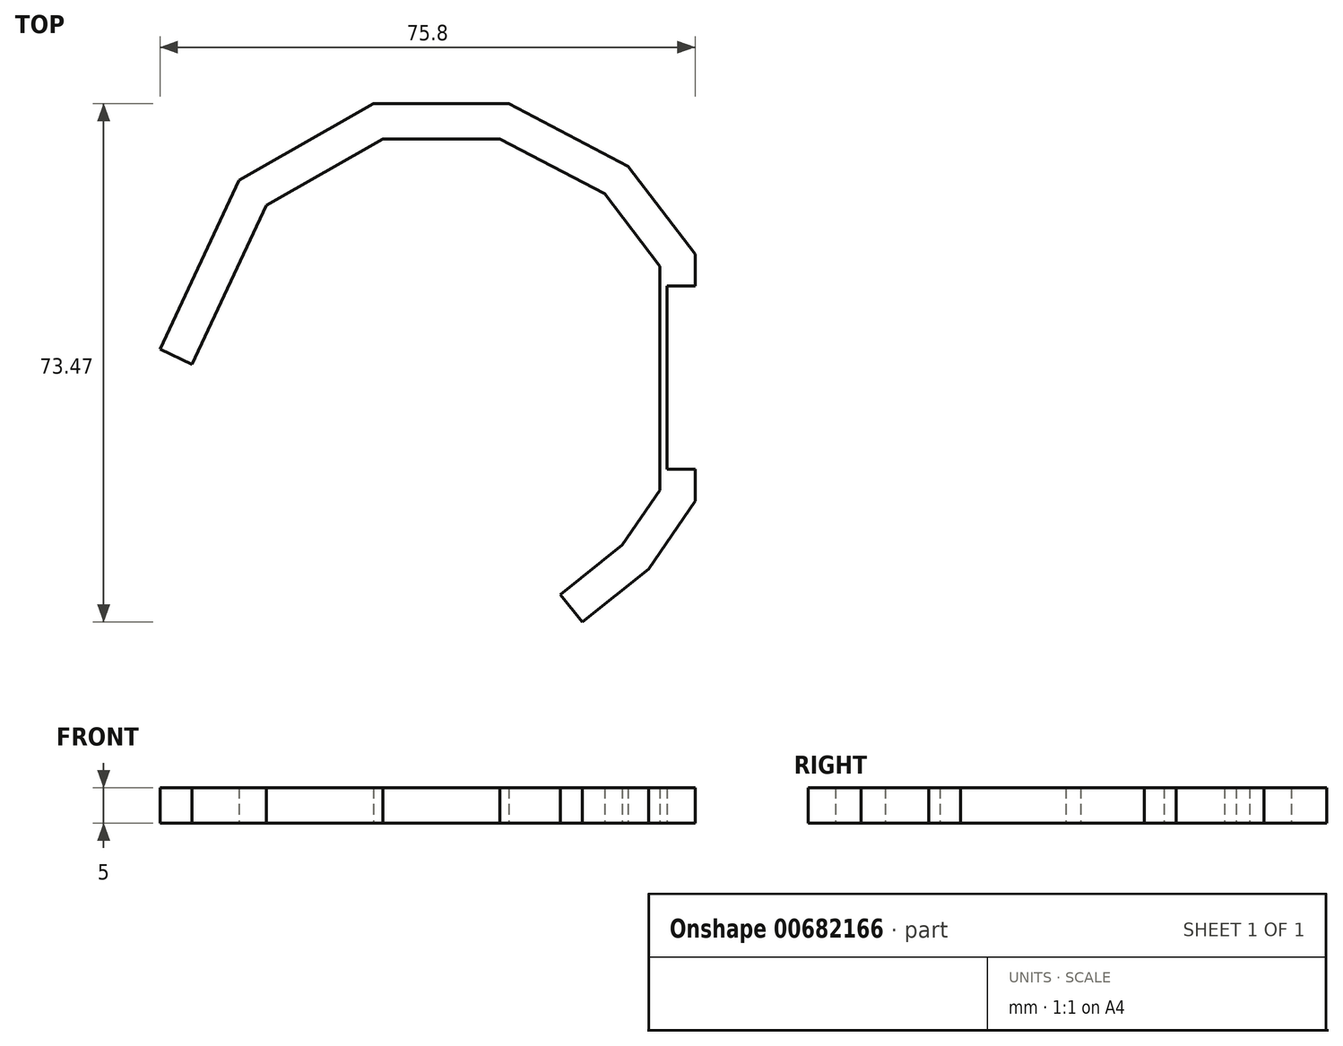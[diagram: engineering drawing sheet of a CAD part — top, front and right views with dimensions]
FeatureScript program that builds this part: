
annotation { "Feature Type Name" : "Feature", "Feature Type Description" : "" }
export const myFeature = defineFeature(function(context is Context, id is Id, definition is map)
    precondition{}
    {
        {
            var Q0;
            Q0=qCreatedBy(makeId("Top.planeOp"),FACE);
            var sketch = newSketch(context, id + "F0", { "sketchPlane" : qUnion([Q0])});
            skLineSegment(sketch, "E0", {"start": v(0, 0) * mm, "end": v(0, -35) * mm});
            skLineSegment(sketch, "E1", {"start": v(0, -35) * mm, "end": v(-6.6, -44.62) * mm});
            skLineSegment(sketch, "E2", {"start": v(-6.6, -44.62) * mm, "end": v(-15.99, -52.13) * mm});
            skLineSegment(sketch, "E3", {"start": v(0, 0) * mm, "end": v(-9.51, 12.47) * mm});
            skLineSegment(sketch, "E4", {"start": v(-9.51, 12.47) * mm, "end": v(-26.42, 21.34) * mm});
            skCircle(sketch, "E5", {"center": v(-36, -17.5) * mm, "radius": 40 * mm, "construction": true});
            skLineSegment(sketch, "E6", {"start": v(-26.42, 21.34) * mm, "end": v(-45.58, 21.34) * mm});
            skLineSegment(sketch, "E7", {"start": v(-45.58, 21.34) * mm, "end": v(-64.6, 10.47) * mm});
            skLineSegment(sketch, "E8", {"start": v(-64.6, 10.47) * mm, "end": v(-75.8, -13.47) * mm});
            skLineSegment(sketch, "E9.0", {"start": v(-60.74, 6.91) * mm, "end": v(-71.27, -15.59) * mm});
            skLineSegment(sketch, "E9.1", {"start": v(-44.25, 16.34) * mm, "end": v(-60.74, 6.91) * mm});
            skLineSegment(sketch, "E9.2", {"start": v(-27.65, 16.34) * mm, "end": v(-44.25, 16.34) * mm});
            skLineSegment(sketch, "E9.3", {"start": v(-12.81, 8.56) * mm, "end": v(-27.65, 16.34) * mm});
            skLineSegment(sketch, "E9.4", {"start": v(-10.3, -41.18) * mm, "end": v(-19.11, -48.23) * mm});
            skLineSegment(sketch, "E9.5", {"start": v(-5, -33.45) * mm, "end": v(-10.3, -41.18) * mm});
            skLineSegment(sketch, "E9.6", {"start": v(-5, -1.69) * mm, "end": v(-5, -33.45) * mm});
            skLineSegment(sketch, "E9.7", {"start": v(-5, -1.69) * mm, "end": v(-12.81, 8.56) * mm});
            skLineSegment(sketch, "E10", {"start": v(-75.8, -13.47) * mm, "end": v(-71.27, -15.59) * mm});
            skLineSegment(sketch, "E11", {"start": v(-19.11, -48.23) * mm, "end": v(-15.99, -52.13) * mm});
            skSolve(sketch);
        }
        {
            var Q0;
            Q0=makeQuery(id+"F0.imprint","IMPRINT",FACE,{"disambiguationData":[TD([[makeQuery(id+"F0.imprint","IMPRINT",EDGE,{"derivedFrom":sQuery(id+"F0.wireOp",EDGE,"E0")}),-1.0]])]});
            extrude(context, id + "F1", {"entities" : qUnion([Q0]), "depth" : 5 * mm, "offsetDistance" : 25 * mm});
        }
        {
            var Q0;
            Q0=makeQuery(id+"F1.opExtrude","SWEPT_FACE",FACE,{"disambiguationData":[OSD([sQuery(id+"F0.wireOp",EDGE,"E0")])]});
            var sketch = newSketch(context, id + "F2", { "sketchPlane" : qUnion([Q0])});
            skLineSegment(sketch, "E12", {"start": v(-4.5, 2.5) * mm, "end": v(-4.5, 5) * mm});
            skLineSegment(sketch, "E13", {"start": v(-4.5, 2.5) * mm, "end": v(-4.5, 0) * mm});
            skLineSegment(sketch, "E14", {"start": v(-30.5, 2.5) * mm, "end": v(-30.5, 0) * mm});
            skLineSegment(sketch, "E15", {"start": v(-30.5, 2.5) * mm, "end": v(-30.5, 5) * mm});
            skLineSegment(sketch, "E16", {"start": v(-30.5, 0) * mm, "end": v(-4.5, 0) * mm});
            skLineSegment(sketch, "E17", {"start": v(-30.5, 5) * mm, "end": v(-4.5, 5) * mm});
            skSolve(sketch);
        }
        {
            var Q0;
            Q0=makeQuery(id+"F2.imprint","IMPRINT",FACE,{"disambiguationData":[TD([[makeQuery(id+"F2.imprint","IMPRINT",EDGE,{"derivedFrom":sQuery(id+"F2.wireOp",EDGE,"E12")}),1.0]])]});
            extrude(context, id + "F3", {"entities" : qUnion([Q0]), "operationType" : NewBodyOperationType.REMOVE, "oppositeDirection" : true, "depth" : 4 * mm, "offsetDistance" : 25 * mm});
        }
        {
            var Q0;
            Q0=makeQuery(id+"F1.opExtrude","SWEPT_BODY",BODY,{"disambiguationData":[OSD([sQuery(id+"F0.wireOp",EDGE,"E0"),sQuery(id+"F0.wireOp",EDGE,"E1"),sQuery(id+"F0.wireOp",EDGE,"E2"),sQuery(id+"F0.wireOp",EDGE,"E3"),sQuery(id+"F0.wireOp",EDGE,"E4"),sQuery(id+"F0.wireOp",EDGE,"E6"),sQuery(id+"F0.wireOp",EDGE,"E7"),sQuery(id+"F0.wireOp",EDGE,"E8"),sQuery(id+"F0.wireOp",EDGE,"E9.0"),sQuery(id+"F0.wireOp",EDGE,"E9.1"),sQuery(id+"F0.wireOp",EDGE,"E9.2"),sQuery(id+"F0.wireOp",EDGE,"E9.3"),sQuery(id+"F0.wireOp",EDGE,"E9.4"),sQuery(id+"F0.wireOp",EDGE,"E9.5"),sQuery(id+"F0.wireOp",EDGE,"E9.6"),sQuery(id+"F0.wireOp",EDGE,"E9.7"),sQuery(id+"F0.wireOp",EDGE,"E10"),sQuery(id+"F0.wireOp",EDGE,"E11")])]});
            transform(context, id + "F4", {"entities" : qUnion([Q0]), "transformType" : TransformType.TRANSLATION_3D, "dx" : 0 * mm, "dy" : 0 * mm, "dz" : 0 * mm, "makeCopy" : true});
        }
        {
            var Q0;
            Q0=makeQuery(id+"F1.opExtrude","SWEPT_BODY",BODY,{"disambiguationData":[OSD([sQuery(id+"F0.wireOp",EDGE,"E0"),sQuery(id+"F0.wireOp",EDGE,"E1"),sQuery(id+"F0.wireOp",EDGE,"E2"),sQuery(id+"F0.wireOp",EDGE,"E3"),sQuery(id+"F0.wireOp",EDGE,"E4"),sQuery(id+"F0.wireOp",EDGE,"E6"),sQuery(id+"F0.wireOp",EDGE,"E7"),sQuery(id+"F0.wireOp",EDGE,"E8"),sQuery(id+"F0.wireOp",EDGE,"E9.0"),sQuery(id+"F0.wireOp",EDGE,"E9.1"),sQuery(id+"F0.wireOp",EDGE,"E9.2"),sQuery(id+"F0.wireOp",EDGE,"E9.3"),sQuery(id+"F0.wireOp",EDGE,"E9.4"),sQuery(id+"F0.wireOp",EDGE,"E9.5"),sQuery(id+"F0.wireOp",EDGE,"E9.6"),sQuery(id+"F0.wireOp",EDGE,"E9.7"),sQuery(id+"F0.wireOp",EDGE,"E10"),sQuery(id+"F0.wireOp",EDGE,"E11")])]});
            deleteBodies(context, id + "F5", {"entities" : qUnion([Q0])});
        }
    });
